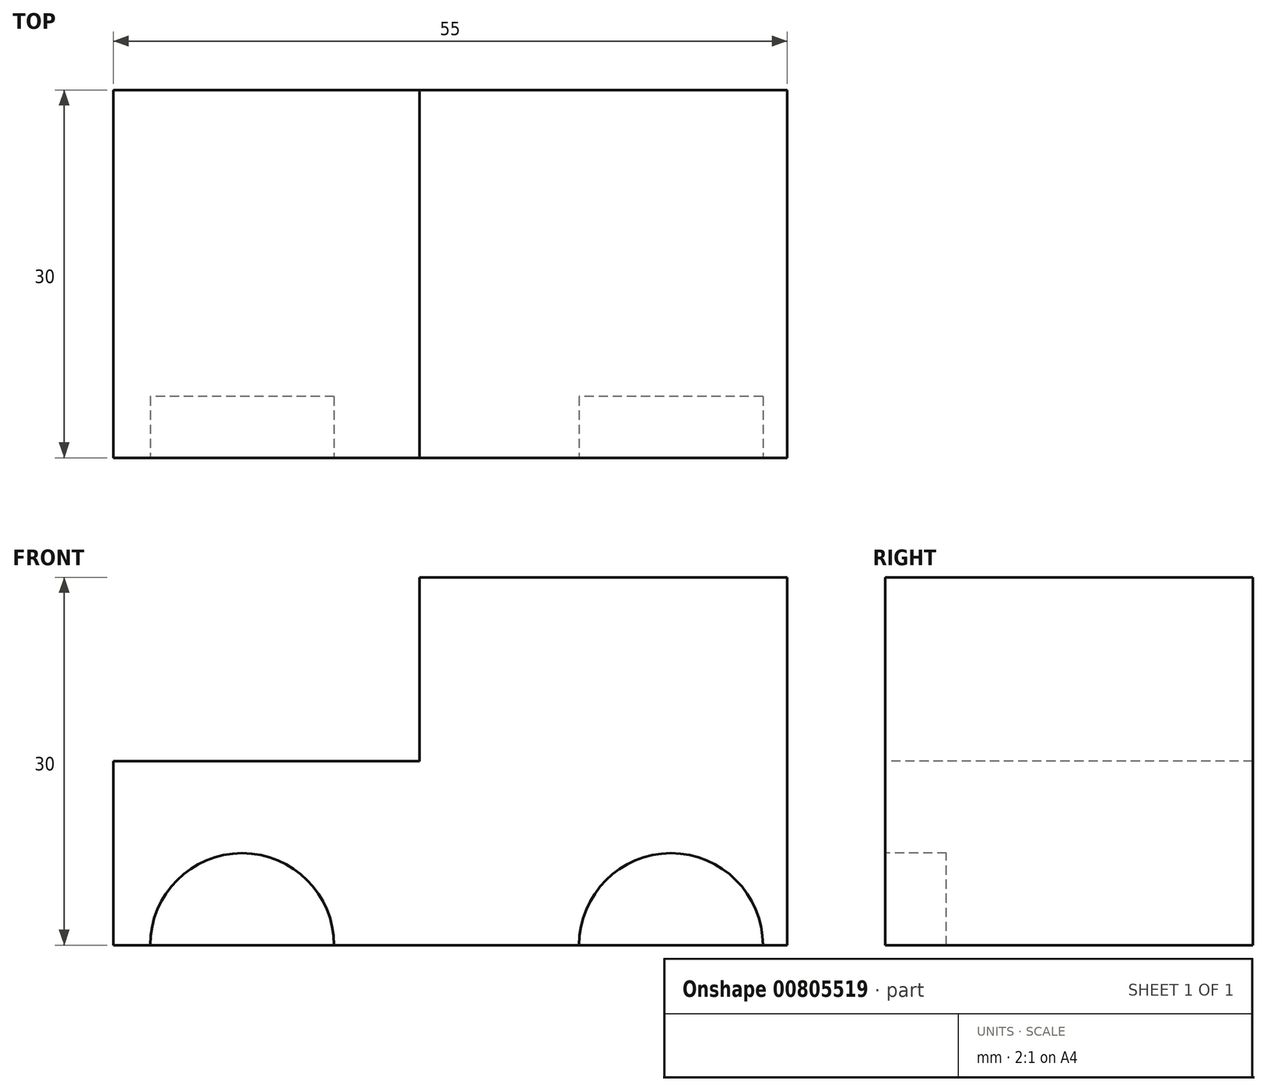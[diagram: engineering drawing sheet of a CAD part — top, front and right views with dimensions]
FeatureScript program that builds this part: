
annotation { "Feature Type Name" : "Feature", "Feature Type Description" : "" }
export const myFeature = defineFeature(function(context is Context, id is Id, definition is map)
    precondition{}
    {
        {
            var Q0;
            Q0=qCreatedBy(makeId("Top.planeOp"),FACE);
            var sketch = newSketch(context, id + "F0", { "sketchPlane" : qUnion([Q0])});
            skLineSegment(sketch, "E0.bottom", {"start": v(27.5, 15) * mm, "end": v(-27.5, 15) * mm});
            skLineSegment(sketch, "E0.top", {"start": v(27.5, -15) * mm, "end": v(-27.5, -15) * mm});
            skLineSegment(sketch, "E0.left", {"start": v(27.5, 15) * mm, "end": v(27.5, -15) * mm});
            skLineSegment(sketch, "E0.right", {"start": v(-27.5, 15) * mm, "end": v(-27.5, -15) * mm});
            skPoint(sketch, "E0.middle", {"position": v(0, 0) * mm});
            skSolve(sketch);
        }
        {
            var Q0;
            Q0 = qSketchRegion(id + "F0", true);
            extrude(context, id + "F1", {"entities" : qUnion([Q0]), "depth" : 30 * mm, "offsetDistance" : 25 * mm});
        }
        {
            var Q0;
            Q0=makeQuery(id+"F1.opExtrude","SWEPT_FACE",FACE,{"disambiguationData":[OSD([sQuery(id+"F0.wireOp",EDGE,"E0.top")])]});
            var sketch = newSketch(context, id + "F2", { "sketchPlane" : qUnion([Q0])});
            skLineSegment(sketch, "E1.bottom", {"start": v(-27.5, 30) * mm, "end": v(-2.5, 30) * mm});
            skLineSegment(sketch, "E1.top", {"start": v(-27.5, 15) * mm, "end": v(-2.5, 15) * mm});
            skLineSegment(sketch, "E1.left", {"start": v(-27.5, 30) * mm, "end": v(-27.5, 15) * mm});
            skLineSegment(sketch, "E1.right", {"start": v(-2.5, 30) * mm, "end": v(-2.5, 15) * mm});
            skSolve(sketch);
        }
        {
            var Q0;
            Q0=makeQuery(id+"F2.imprint","IMPRINT",FACE,{"disambiguationData":[TD([[makeQuery(id+"F2.imprint","IMPRINT",EDGE,{"derivedFrom":sQuery(id+"F2.wireOp",EDGE,"E1.bottom")}),1.0]])]});
            extrude(context, id + "F3", {"entities" : qUnion([Q0]), "operationType" : NewBodyOperationType.REMOVE, "endBound" : BoundingType.THROUGH_ALL, "oppositeDirection" : true, "depth" : 25 * mm, "offsetDistance" : 25 * mm});
        }
        {
            var Q0;
            Q0=makeQuery(id+"F1.opExtrude","SWEPT_FACE",FACE,{"disambiguationData":[OSD([sQuery(id+"F0.wireOp",EDGE,"E0.top")])]});
            var sketch = newSketch(context, id + "F4", { "sketchPlane" : qUnion([Q0])});
            skCircle(sketch, "E2", {"center": v(-16.98, 0) * mm, "radius": 7.5 * mm});
            skCircle(sketch, "E3.1.0.0", {"center": v(18.02, 0) * mm, "radius": 7.5 * mm});
            skLineSegment(sketch, "E3.direction1", {"start": v(-16.98, 0) * mm, "end": v(18.02, 0) * mm, "construction": true});
            skSolve(sketch);
        }
        {
            var Q0;
            {var subQ0=sQuery(id+"F4.wireOp",EDGE,"E2");var subQ1=makeQuery(id+"F1.opExtrude","CAP_EDGE",EDGE,{"disambiguationData":[OSD([sQuery(id+"F0.wireOp",EDGE,"E0.top")])],"isStart":true});var subQ2=makeQuery(id+"F4.imprint","INTERSECT",VERTEX,{"disambiguationData":[OD(0.0)],"derivedFrom":[subQ1,subQ0]});Q0=makeQuery(id+"F4.imprint","IMPRINT",FACE,{"disambiguationData":[TD([[makeQuery(id+"F4.imprint","IMPRINT",EDGE,{"disambiguationData":[TD([[subQ2,1.0]])],"derivedFrom":subQ0}),1.0]])]});}
            var Q1;
            {var subQ0=sQuery(id+"F4.wireOp",EDGE,"E3.1.0.0");var subQ1=makeQuery(id+"F1.opExtrude","CAP_EDGE",EDGE,{"disambiguationData":[OSD([sQuery(id+"F0.wireOp",EDGE,"E0.top")])],"isStart":true});var subQ2=makeQuery(id+"F4.imprint","INTERSECT",VERTEX,{"disambiguationData":[OD(0.0)],"derivedFrom":[subQ1,subQ0]});Q1=makeQuery(id+"F4.imprint","IMPRINT",FACE,{"disambiguationData":[TD([[makeQuery(id+"F4.imprint","IMPRINT",EDGE,{"disambiguationData":[TD([[subQ2,-1.0]])],"derivedFrom":subQ0}),1.0]])]});}
            extrude(context, id + "F5", {"entities" : qUnion([Q0, Q1]), "operationType" : NewBodyOperationType.REMOVE, "oppositeDirection" : true, "depth" : 5 * mm, "offsetDistance" : 25 * mm});
        }
    });
